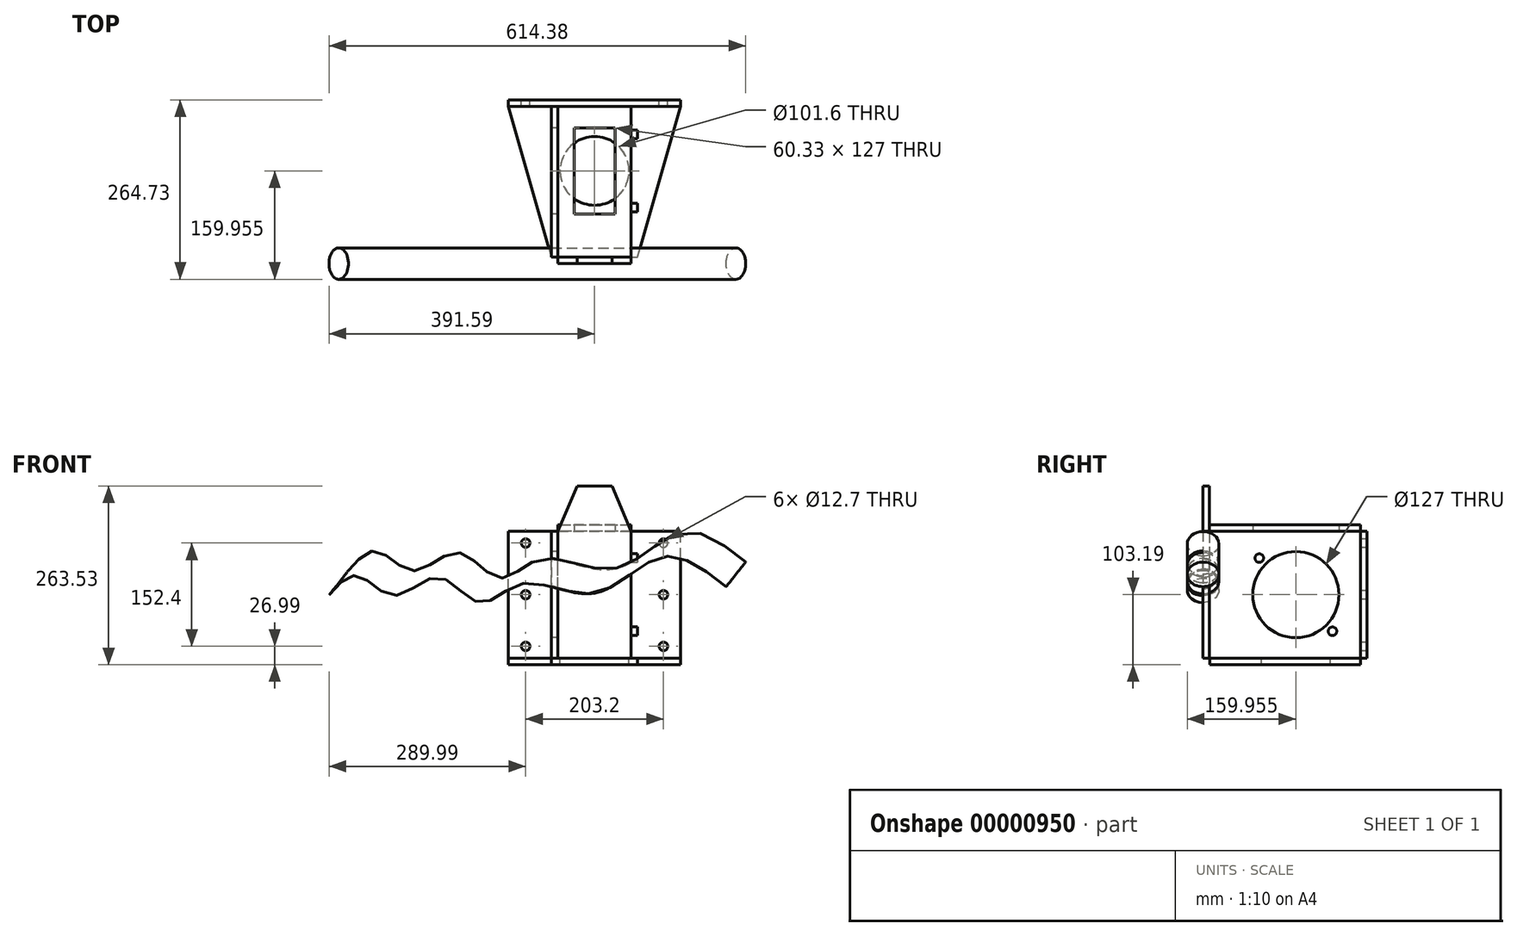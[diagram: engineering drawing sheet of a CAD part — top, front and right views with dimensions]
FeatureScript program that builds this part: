
annotation { "Feature Type Name" : "Feature", "Feature Type Description" : "" }
export const myFeature = defineFeature(function(context is Context, id is Id, definition is map)
    precondition{}
    {
        {
            var Q0;
            Q0=qCreatedBy(makeId("Front.planeOp"),FACE);
            var sketch = newSketch(context, id + "F0", { "sketchPlane" : qUnion([Q0])});
            skLineSegment(sketch, "E0.rect.bottom", {"start": v(127, -93.66) * mm, "end": v(-127, -93.66) * mm});
            skLineSegment(sketch, "E0.rect.top", {"start": v(127, 93.66) * mm, "end": v(-127, 93.66) * mm});
            skLineSegment(sketch, "E0.rect.left", {"start": v(127, -93.66) * mm, "end": v(127, 93.66) * mm});
            skLineSegment(sketch, "E0.rect.right", {"start": v(-127, -93.66) * mm, "end": v(-127, 93.66) * mm});
            skPoint(sketch, "E0.rect.middle", {"position": v(0, 0) * mm});
            skLineSegment(sketch, "E1", {"start": v(-101.6, 93.66) * mm, "end": v(-101.6, -93.66) * mm, "construction": true});
            skCircle(sketch, "E2", {"center": v(-101.6, 0) * mm, "radius": 6.35 * mm});
            skCircle(sketch, "E3", {"center": v(-101.6, 76.2) * mm, "radius": 6.35 * mm});
            skCircle(sketch, "E4", {"center": v(-101.6, -76.2) * mm, "radius": 6.35 * mm});
            skLineSegment(sketch, "E5", {"start": v(0, 0) * mm, "end": v(0, 93.66) * mm, "construction": true});
            skCircle(sketch, "E6.0.MirrorC", {"center": v(101.6, 76.2) * mm, "radius": 6.35 * mm});
            skCircle(sketch, "E7.0.MirrorC", {"center": v(101.6, 0) * mm, "radius": 6.35 * mm});
            skCircle(sketch, "E8.0.MirrorC", {"center": v(101.6, -76.2) * mm, "radius": 6.35 * mm});
            skSolve(sketch);
        }
        {
            var Q0;
            Q0=makeQuery(id+"F0.imprint","IMPRINT",FACE,{"disambiguationData":[TD([[makeQuery(id+"F0.imprint","IMPRINT",EDGE,{"derivedFrom":sQuery(id+"F0.wireOp",EDGE,"E0.rect.bottom")}),-1.0]])]});
            extrude(context, id + "F1", {"entities" : qUnion([Q0]), "depth" : 9.52 * mm});
        }
        {
            var Q0;
            Q0=makeQuery(id+"F1.opExtrude","SWEPT_FACE",FACE,{"disambiguationData":[OSD([sQuery(id+"F0.wireOp",EDGE,"E0.rect.bottom")])]});
            var sketch = newSketch(context, id + "F2", { "sketchPlane" : qUnion([Q0])});
            skLineSegment(sketch, "E9", {"start": v(-127, 0) * mm, "end": v(-63.5, -222.25) * mm});
            skLineSegment(sketch, "E10", {"start": v(-63.5, -222.25) * mm, "end": v(63.5, -222.25) * mm});
            skLineSegment(sketch, "E11", {"start": v(63.5, -222.25) * mm, "end": v(127, 0) * mm});
            skLineSegment(sketch, "E12", {"start": v(0, 0) * mm, "end": v(0, -222.25) * mm, "construction": true});
            skCircle(sketch, "E13", {"center": v(0, -95.25) * mm, "radius": 50.8 * mm});
            skSolve(sketch);
        }
        {
            var Q0;
            Q0=makeQuery(id+"F2.imprint","IMPRINT",FACE,{"disambiguationData":[TD([[makeQuery(id+"F2.imprint","IMPRINT",EDGE,{"derivedFrom":sQuery(id+"F2.wireOp",EDGE,"E9")}),1.0]])]});
            extrude(context, id + "F3", {"entities" : qUnion([Q0]), "depth" : 9.52 * mm});
        }
        {
            var Q0;
            Q0=makeQuery(id+"F1.opExtrude","CAP_FACE",FACE,{"disambiguationData":[OSD([sQuery(id+"F0.wireOp",EDGE,"E0.rect.bottom"),sQuery(id+"F0.wireOp",EDGE,"E0.rect.top"),sQuery(id+"F0.wireOp",EDGE,"E0.rect.left"),sQuery(id+"F0.wireOp",EDGE,"E0.rect.right"),sQuery(id+"F0.wireOp",EDGE,"E2"),sQuery(id+"F0.wireOp",EDGE,"E3"),sQuery(id+"F0.wireOp",EDGE,"E4"),sQuery(id+"F0.wireOp",EDGE,"E6.0.MirrorC"),sQuery(id+"F0.wireOp",EDGE,"E7.0.MirrorC"),sQuery(id+"F0.wireOp",EDGE,"E8.0.MirrorC")])],"isStart":false});
            var Q1;
            Q1=makeQuery(id+"F1.opExtrude","CAP_FACE",FACE,{"disambiguationData":[OSD([sQuery(id+"F0.wireOp",EDGE,"E0.rect.bottom"),sQuery(id+"F0.wireOp",EDGE,"E0.rect.top"),sQuery(id+"F0.wireOp",EDGE,"E0.rect.left"),sQuery(id+"F0.wireOp",EDGE,"E0.rect.right"),sQuery(id+"F0.wireOp",EDGE,"E2"),sQuery(id+"F0.wireOp",EDGE,"E3"),sQuery(id+"F0.wireOp",EDGE,"E4"),sQuery(id+"F0.wireOp",EDGE,"E6.0.MirrorC"),sQuery(id+"F0.wireOp",EDGE,"E7.0.MirrorC"),sQuery(id+"F0.wireOp",EDGE,"E8.0.MirrorC")])],"isStart":true});
            cPlane(context, id + "F4", {"entities" : qUnion([Q0, Q1]), "cplaneType" : CPlaneType.MID_PLANE, "offset" : 152.4 * mm, "width" : 152.4 * mm, "height" : 152.4 * mm});
        }
        {
            var Q0;
            Q0=makeQuery(id+"F3.opExtrude","SWEPT_BODY",BODY,{"disambiguationData":[OSD([sQuery(id+"F0.wireOp",EDGE,"E0.rect.bottom"),sQuery(id+"F2.wireOp",EDGE,"E9"),sQuery(id+"F2.wireOp",EDGE,"E10"),sQuery(id+"F2.wireOp",EDGE,"E11"),sQuery(id+"F2.wireOp",EDGE,"E13")])]});
            var Q1;
            Q1=qCreatedBy(id+"F4.planeOp",FACE);
            mirror(context, id + "F5", {"entities" : qUnion([Q0]), "mirrorPlane" : qUnion([Q1])});
        }
        {
            var Q0;
            Q0=makeQuery(id+"F3.opExtrude","SWEPT_BODY",BODY,{"disambiguationData":[OSD([sQuery(id+"F0.wireOp",EDGE,"E0.rect.bottom"),sQuery(id+"F2.wireOp",EDGE,"E9"),sQuery(id+"F2.wireOp",EDGE,"E10"),sQuery(id+"F2.wireOp",EDGE,"E11"),sQuery(id+"F2.wireOp",EDGE,"E13")])]});
            deleteBodies(context, id + "F6", {"entities" : qUnion([Q0])});
        }
        {
            var Q0;
            Q0=makeQuery(id+"F1.opExtrude","CAP_FACE",FACE,{"disambiguationData":[OSD([sQuery(id+"F0.wireOp",EDGE,"E0.rect.bottom"),sQuery(id+"F0.wireOp",EDGE,"E0.rect.top"),sQuery(id+"F0.wireOp",EDGE,"E0.rect.left"),sQuery(id+"F0.wireOp",EDGE,"E0.rect.right"),sQuery(id+"F0.wireOp",EDGE,"E2"),sQuery(id+"F0.wireOp",EDGE,"E3"),sQuery(id+"F0.wireOp",EDGE,"E4"),sQuery(id+"F0.wireOp",EDGE,"E6.0.MirrorC"),sQuery(id+"F0.wireOp",EDGE,"E7.0.MirrorC"),sQuery(id+"F0.wireOp",EDGE,"E8.0.MirrorC")])],"isStart":false});
            var sketch = newSketch(context, id + "F7", { "sketchPlane" : qUnion([Q0])});
            skLineSegment(sketch, "E14", {"start": v(0, 93.66) * mm, "end": v(0, -93.66) * mm, "construction": true});
            skLineSegment(sketch, "E15.bottom", {"start": v(-53.98, 93.66) * mm, "end": v(-63.5, 93.66) * mm});
            skLineSegment(sketch, "E15.top", {"start": v(-53.97, -93.66) * mm, "end": v(-63.5, -93.66) * mm});
            skLineSegment(sketch, "E15.left", {"start": v(-53.98, 93.66) * mm, "end": v(-53.97, -93.66) * mm});
            skLineSegment(sketch, "E15.right", {"start": v(-63.5, 93.66) * mm, "end": v(-63.5, -93.66) * mm});
            skLineSegment(sketch, "E16.0.MirrorCS", {"start": v(53.97, 93.66) * mm, "end": v(53.98, -93.66) * mm});
            skLineSegment(sketch, "E16.1.MirrorCS", {"start": v(63.5, 93.66) * mm, "end": v(63.5, -93.66) * mm});
            skLineSegment(sketch, "E16.2.MirrorCS", {"start": v(53.97, 93.66) * mm, "end": v(63.5, 93.66) * mm});
            skLineSegment(sketch, "E16.3.MirrorCS", {"start": v(53.98, -93.66) * mm, "end": v(63.5, -93.66) * mm});
            skSolve(sketch);
        }
        {
            var Q0;
            Q0=makeQuery(id+"F7.imprint","IMPRINT",FACE,{"disambiguationData":[TD([[makeQuery(id+"F7.imprint","IMPRINT",EDGE,{"derivedFrom":sQuery(id+"F7.wireOp",EDGE,"E15.bottom")}),1.0]])]});
            var Q1;
            Q1=makeQuery(id+"F7.imprint","IMPRINT",FACE,{"disambiguationData":[TD([[makeQuery(id+"F7.imprint","IMPRINT",EDGE,{"derivedFrom":sQuery(id+"F7.wireOp",EDGE,"E16.0.MirrorCS")}),1.0]])]});
            extrude(context, id + "F8", {"entities" : qUnion([Q0, Q1]), "depth" : 222.5 * mm});
        }
        {
            var Q0;
            Q0=makeQuery(id+"F8.opExtrude","SWEPT_FACE",FACE,{"disambiguationData":[OSD([sQuery(id+"F7.wireOp",EDGE,"E16.1.MirrorCS")])]});
            var sketch = newSketch(context, id + "F9", { "sketchPlane" : qUnion([Q0])});
            skLineSegment(sketch, "E17", {"start": v(-232.03, 0) * mm, "end": v(-9.53, 0) * mm, "construction": true});
            skCircle(sketch, "E18", {"center": v(-104.78, 0) * mm, "radius": 63.5 * mm});
            skLineSegment(sketch, "E19", {"start": v(-104.78, 0) * mm, "end": v(-104.78, -97.65) * mm, "construction": true});
            skCircle(sketch, "E20", {"center": v(-158.75, -53.98) * mm, "radius": 6.35 * mm});
            skCircle(sketch, "E21.0.MirrorC", {"center": v(-50.8, -53.98) * mm, "radius": 6.35 * mm});
            skCircle(sketch, "E22.0.MirrorC", {"center": v(-50.8, 53.98) * mm, "radius": 6.35 * mm});
            skCircle(sketch, "E23.0.MirrorC", {"center": v(-158.75, 53.98) * mm, "radius": 6.35 * mm});
            skSolve(sketch);
        }
        {
            var Q0;
            Q0=makeQuery(id+"F9.imprint","IMPRINT",FACE,{"disambiguationData":[TD([[makeQuery(id+"F9.imprint","IMPRINT",EDGE,{"derivedFrom":sQuery(id+"F9.wireOp",EDGE,"E23.0.MirrorC")}),-1.0]])]});
            var Q1;
            Q1=makeQuery(id+"F9.imprint","IMPRINT",FACE,{"disambiguationData":[TD([[makeQuery(id+"F9.imprint","IMPRINT",EDGE,{"derivedFrom":sQuery(id+"F9.wireOp",EDGE,"E18")}),1.0]])]});
            var Q2;
            Q2=makeQuery(id+"F9.imprint","IMPRINT",FACE,{"disambiguationData":[TD([[makeQuery(id+"F9.imprint","IMPRINT",EDGE,{"derivedFrom":sQuery(id+"F9.wireOp",EDGE,"E22.0.MirrorC")}),1.0]])]});
            var Q3;
            Q3=makeQuery(id+"F9.imprint","IMPRINT",FACE,{"disambiguationData":[TD([[makeQuery(id+"F9.imprint","IMPRINT",EDGE,{"derivedFrom":sQuery(id+"F9.wireOp",EDGE,"E21.0.MirrorC")}),-1.0]])]});
            var Q4;
            Q4=makeQuery(id+"F9.imprint","IMPRINT",FACE,{"disambiguationData":[TD([[makeQuery(id+"F9.imprint","IMPRINT",EDGE,{"derivedFrom":sQuery(id+"F9.wireOp",EDGE,"E20")}),1.0]])]});
            extrude(context, id + "F10", {"entities" : qUnion([Q0, Q1, Q2, Q3, Q4]), "operationType" : NewBodyOperationType.REMOVE, "oppositeDirection" : true, "depth" : 25.4 * mm});
        }
        {
            var Q0;
            Q0=makeQuery(id+"F8.opExtrude","SWEPT_FACE",FACE,{"disambiguationData":[OSD([sQuery(id+"F7.wireOp",EDGE,"E15.right")])]});
            var sketch = newSketch(context, id + "F11", { "sketchPlane" : qUnion([Q0])});
            skCircle(sketch, "E24", {"center": v(104.78, 0) * mm, "radius": 63.5 * mm});
            skSolve(sketch);
        }
        {
            var Q0;
            Q0=makeQuery(id+"F11.imprint","IMPRINT",FACE,{"disambiguationData":[TD([[makeQuery(id+"F11.imprint","IMPRINT",EDGE,{"derivedFrom":sQuery(id+"F11.wireOp",EDGE,"E24")}),1.0]])]});
            extrude(context, id + "F12", {"entities" : qUnion([Q0]), "operationType" : NewBodyOperationType.REMOVE, "oppositeDirection" : true, "depth" : 25.4 * mm});
        }
        {
            var Q0;
            Q0=makeQuery(id+"F8.opExtrude","CAP_FACE",FACE,{"disambiguationData":[OSD([sQuery(id+"F7.wireOp",EDGE,"E15.bottom"),sQuery(id+"F7.wireOp",EDGE,"E15.top"),sQuery(id+"F7.wireOp",EDGE,"E15.left"),sQuery(id+"F7.wireOp",EDGE,"E15.right")])],"isStart":false});
            var sketch = newSketch(context, id + "F13", { "sketchPlane" : qUnion([Q0])});
            skLineSegment(sketch, "E25", {"start": v(-53.98, -93.66) * mm, "end": v(-53.98, 93.66) * mm});
            skLineSegment(sketch, "E26", {"start": v(-53.97, 93.66) * mm, "end": v(-25.88, 160.34) * mm});
            skLineSegment(sketch, "E27", {"start": v(-25.88, 160.34) * mm, "end": v(25.88, 160.34) * mm});
            skLineSegment(sketch, "E28", {"start": v(25.88, 160.34) * mm, "end": v(53.97, 93.66) * mm});
            skLineSegment(sketch, "E29", {"start": v(53.97, 93.66) * mm, "end": v(53.98, -93.66) * mm});
            skLineSegment(sketch, "E30", {"start": v(-53.97, 93.66) * mm, "end": v(53.97, 93.66) * mm});
            skLineSegment(sketch, "E31", {"start": v(0, 93.66) * mm, "end": v(0, 160.34) * mm});
            skLineSegment(sketch, "E32", {"start": v(-53.98, -93.66) * mm, "end": v(53.98, -93.66) * mm});
            skSolve(sketch);
        }
        {
            var Q0;
            {var subQ2=sQuery(id+"F13.wireOp",EDGE,"E26");Q0=makeQuery(id+"F13.imprint","IMPRINT",FACE,{"disambiguationData":[TD([[makeQuery(id+"F13.imprint","IMPRINT",EDGE,{"derivedFrom":subQ2}),-1.0]])]});}
            var Q1;
            {var subQ2=sQuery(id+"F13.wireOp",EDGE,"E28");Q1=makeQuery(id+"F13.imprint","IMPRINT",FACE,{"disambiguationData":[TD([[makeQuery(id+"F13.imprint","IMPRINT",EDGE,{"derivedFrom":subQ2}),-1.0]])]});}
            var Q2;
            {var subQ3=sQuery(id+"F13.wireOp",EDGE,"E25");Q2=makeQuery(id+"F13.imprint","IMPRINT",FACE,{"disambiguationData":[TD([[makeQuery(id+"F13.imprint","IMPRINT",EDGE,{"derivedFrom":subQ3}),1.0]])]});}
            extrude(context, id + "F14", {"entities" : qUnion([Q0, Q1, Q2]), "depth" : 9.52 * mm});
        }
        {
            var Q0;
            Q0=makeQuery(id+"F8.opExtrude","SWEPT_FACE",FACE,{"disambiguationData":[OSD([sQuery(id+"F7.wireOp",EDGE,"E15.bottom")])]});
            var sketch = newSketch(context, id + "F15", { "sketchPlane" : qUnion([Q0])});
            skLineSegment(sketch, "E33.bottom", {"start": v(-53.97, -9.53) * mm, "end": v(53.97, -9.53) * mm});
            skLineSegment(sketch, "E33.top", {"start": v(-53.97, -232.03) * mm, "end": v(53.97, -232.03) * mm});
            skLineSegment(sketch, "E33.left", {"start": v(-53.97, -9.53) * mm, "end": v(-53.97, -232.03) * mm});
            skLineSegment(sketch, "E33.right", {"start": v(53.97, -9.53) * mm, "end": v(53.98, -232.03) * mm});
            skLineSegment(sketch, "E34", {"start": v(0, -232.03) * mm, "end": v(0, -9.53) * mm, "construction": true});
            skLineSegment(sketch, "E35.rect.bottom", {"start": v(30.16, -41.27) * mm, "end": v(-30.16, -41.27) * mm});
            skLineSegment(sketch, "E35.rect.top", {"start": v(30.16, -168.28) * mm, "end": v(-30.16, -168.28) * mm});
            skLineSegment(sketch, "E35.rect.left", {"start": v(30.16, -41.27) * mm, "end": v(30.16, -168.27) * mm});
            skLineSegment(sketch, "E35.rect.right", {"start": v(-30.16, -41.27) * mm, "end": v(-30.16, -168.28) * mm});
            skPoint(sketch, "E35.rect.middle", {"position": v(0, -104.77) * mm});
            skSolve(sketch);
        }
        {
            var Q0;
            Q0=makeQuery(id+"F15.imprint","IMPRINT",FACE,{"disambiguationData":[TD([[makeQuery(id+"F15.imprint","IMPRINT",EDGE,{"derivedFrom":sQuery(id+"F15.wireOp",EDGE,"E33.bottom")}),-1.0]])]});
            extrude(context, id + "F16", {"entities" : qUnion([Q0]), "depth" : 9.52 * mm});
        }
        {
            var Q0;
            Q0=makeQuery(id+"F14.opExtrude","CAP_FACE",FACE,{"disambiguationData":[OSD([sQuery(id+"F13.wireOp",EDGE,"E25"),sQuery(id+"F13.wireOp",EDGE,"E26"),sQuery(id+"F13.wireOp",EDGE,"E27"),sQuery(id+"F13.wireOp",EDGE,"E28"),sQuery(id+"F13.wireOp",EDGE,"E29"),sQuery(id+"F13.wireOp",EDGE,"E32")])],"isStart":false});
            var sketch = newSketch(context, id + "F17", { "sketchPlane" : qUnion([Q0])});
            skFitSpline(sketch, "E36", {"points": [v(-377.23, 17.56) * mm, v(-334.67, 46.18) * mm, v(-281.1, 16.82) * mm, v(-215.77, 43.98) * mm, v(-155.6, 6.55) * mm, v(-92.47, 34.44) * mm, v(14.68, 20.5) * mm, v(113.76, 74.07) * mm, v(208.43, 30.03) * mm], "startDerivative": vector(412.35, 472.92) * mm, "endDerivative": vector(668.48, -527.48) * mm});
            skSolve(sketch);
        }
        {
            var Q0;
            Q0=sQuery(id+"F17.wireOp",EDGE,"E36");
            var Q1;
            Q1=sQuery(id+"F17.wireOp",VERTEX,"E36.end");
            cPlane(context, id + "F18", {"entities" : qUnion([Q0, Q1]), "cplaneType" : CPlaneType.CURVE_POINT, "offset" : 25.4 * mm, "width" : 152.4 * mm, "height" : 152.4 * mm});
        }
        {
            var Q0;
            Q0=qCreatedBy(id+"F18.planeOp",FACE);
            var sketch = newSketch(context, id + "F19", { "sketchPlane" : qUnion([Q0])});
            skCircle(sketch, "E37", {"center": v(-241.55, 152.7) * mm, "radius": 23.18 * mm});
            skSolve(sketch);
        }
        {
            var Q0;
            Q0=makeQuery(id+"F19.imprint","IMPRINT",FACE,{"disambiguationData":[TD([[makeQuery(id+"F19.imprint","IMPRINT",EDGE,{"derivedFrom":sQuery(id+"F19.wireOp",EDGE,"E37")}),1.0]])]});
            var Q1;
            Q1=sQuery(id+"F17.wireOp",EDGE,"E36");
            sweep(context, id + "F20", {"profiles" : qUnion([Q0]), "path" : qUnion([Q1]), "keepProfileOrientation" : true});
        }
        {
            var Q0;
            Q0=makeQuery(id+"F20.opSweep","SWEPT_BODY",BODY,{"disambiguationData":[OSD([sQuery(id+"F17.wireOp",EDGE,"E36"),sQuery(id+"F19.wireOp",EDGE,"E37")])]});
            var Q1;
            Q1=makeQuery(id+"F8.opExtrude","SWEPT_BODY",BODY,{"disambiguationData":[OSD([sQuery(id+"F7.wireOp",EDGE,"E15.bottom"),sQuery(id+"F7.wireOp",EDGE,"E15.top"),sQuery(id+"F7.wireOp",EDGE,"E15.left"),sQuery(id+"F7.wireOp",EDGE,"E15.right")])]});
            var Q2;
            Q2=makeQuery(id+"F14.opExtrude","SWEPT_BODY",BODY,{"disambiguationData":[OSD([sQuery(id+"F13.wireOp",EDGE,"E25"),sQuery(id+"F13.wireOp",EDGE,"E26"),sQuery(id+"F13.wireOp",EDGE,"E27"),sQuery(id+"F13.wireOp",EDGE,"E28"),sQuery(id+"F13.wireOp",EDGE,"E29"),sQuery(id+"F13.wireOp",EDGE,"E32")])]});
            var Q3;
            Q3=makeQuery(id+"F8.opExtrude","SWEPT_BODY",BODY,{"disambiguationData":[OSD([sQuery(id+"F7.wireOp",EDGE,"E16.0.MirrorCS"),sQuery(id+"F7.wireOp",EDGE,"E16.1.MirrorCS"),sQuery(id+"F7.wireOp",EDGE,"E16.2.MirrorCS"),sQuery(id+"F7.wireOp",EDGE,"E16.3.MirrorCS")])]});
            booleanBodies(context, id + "F21", {"operationType" : BooleanOperationType.SUBTRACTION, "tools" : qUnion([Q0]), "targets" : qUnion([Q1, Q2, Q3]), "keepTools" : true});
        }
    });
